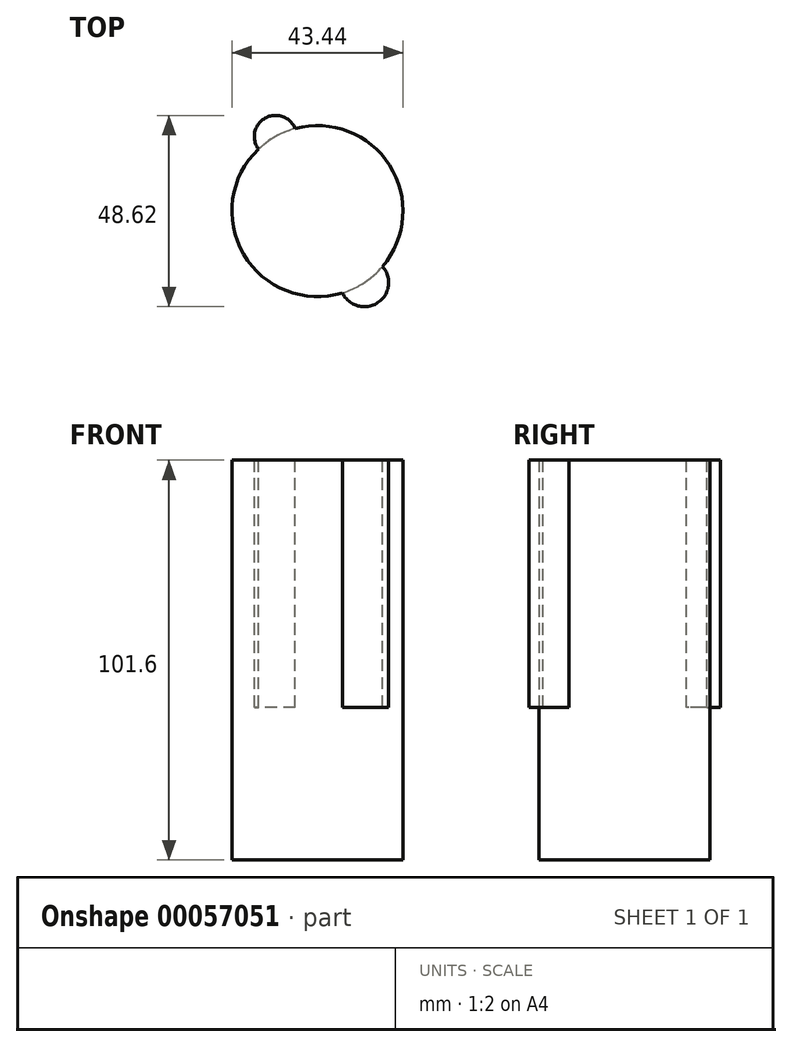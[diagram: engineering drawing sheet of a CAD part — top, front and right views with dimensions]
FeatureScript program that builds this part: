
annotation { "Feature Type Name" : "Feature", "Feature Type Description" : "" }
export const myFeature = defineFeature(function(context is Context, id is Id, definition is map)
    precondition{}
    {
        {
            var Q0;
            Q0=qCreatedBy(makeId("Top.planeOp"),FACE);
            var sketch = newSketch(context, id + "F0", { "sketchPlane" : qUnion([Q0])});
            skSolve(sketch);
        }
        {
            var Q0;
            Q0=qCreatedBy(makeId("Top.planeOp"),FACE);
            var sketch = newSketch(context, id + "F1", { "sketchPlane" : qUnion([Q0])});
            skCircle(sketch, "E0", {"center": v(0, 0) * mm, "radius": 21.72 * mm});
            skSolve(sketch);
        }
        {
            var Q0;
            Q0 = qSketchRegion(id + "F0", true);
            var Q1;
            Q1 = qSketchRegion(id + "FDA9Xdc6rxiplpY_0", true);
            var Q2;
            Q2=makeQuery(id+"F1.imprint","IMPRINT",FACE,{"disambiguationData":[TD([[makeQuery(id+"F1.imprint","IMPRINT",EDGE,{"derivedFrom":sQuery(id+"F1.wireOp",EDGE,"E0")}),1.0]])]});
            extrude(context, id + "F2", {"entities" : qUnion([Q0, Q1, Q2]), "depth" : 101.6 * mm});
        }
        {
            var Q0;
            Q0=makeQuery(id+"F2.opExtrude","CAP_FACE",FACE,{"disambiguationData":[OSD([sQuery(id+"F1.wireOp",EDGE,"E0")])],"isStart":false});
            var sketch = newSketch(context, id + "F3", { "sketchPlane" : qUnion([Q0])});
            skCircle(sketch, "E1", {"center": v(11.94, -18.15) * mm, "radius": 6.16 * mm});
            skCircle(sketch, "E2", {"center": v(-10.65, 18.93) * mm, "radius": 5.39 * mm});
            skSolve(sketch);
        }
        {
            var Q0;
            {var subQ0=sQuery(id+"F3.wireOp",EDGE,"E1");var subQ1=makeQuery(id+"F2.opExtrude","CAP_EDGE",EDGE,{"disambiguationData":[OSD([sQuery(id+"F1.wireOp",EDGE,"E0")])],"isStart":false});var subQ2=makeQuery(id+"F3.imprint","INTERSECT",VERTEX,{"disambiguationData":[OD(0.0)],"derivedFrom":[subQ1,subQ0]});Q0=makeQuery(id+"F3.imprint","IMPRINT",FACE,{"disambiguationData":[TD([[makeQuery(id+"F3.imprint","IMPRINT",EDGE,{"disambiguationData":[TD([[subQ2,1.0]])],"derivedFrom":subQ0}),1.0]])]});}
            extrude(context, id + "F4", {"entities" : qUnion([Q0]), "operationType" : NewBodyOperationType.ADD, "oppositeDirection" : true, "depth" : 99.02 * mm});
        }
        {
            var Q0;
            Q0 = qSketchRegion(id + "F3", true);
            extrude(context, id + "F5", {"entities" : qUnion([Q0]), "operationType" : NewBodyOperationType.ADD, "oppositeDirection" : true, "depth" : 62.77 * mm});
        }
    });
